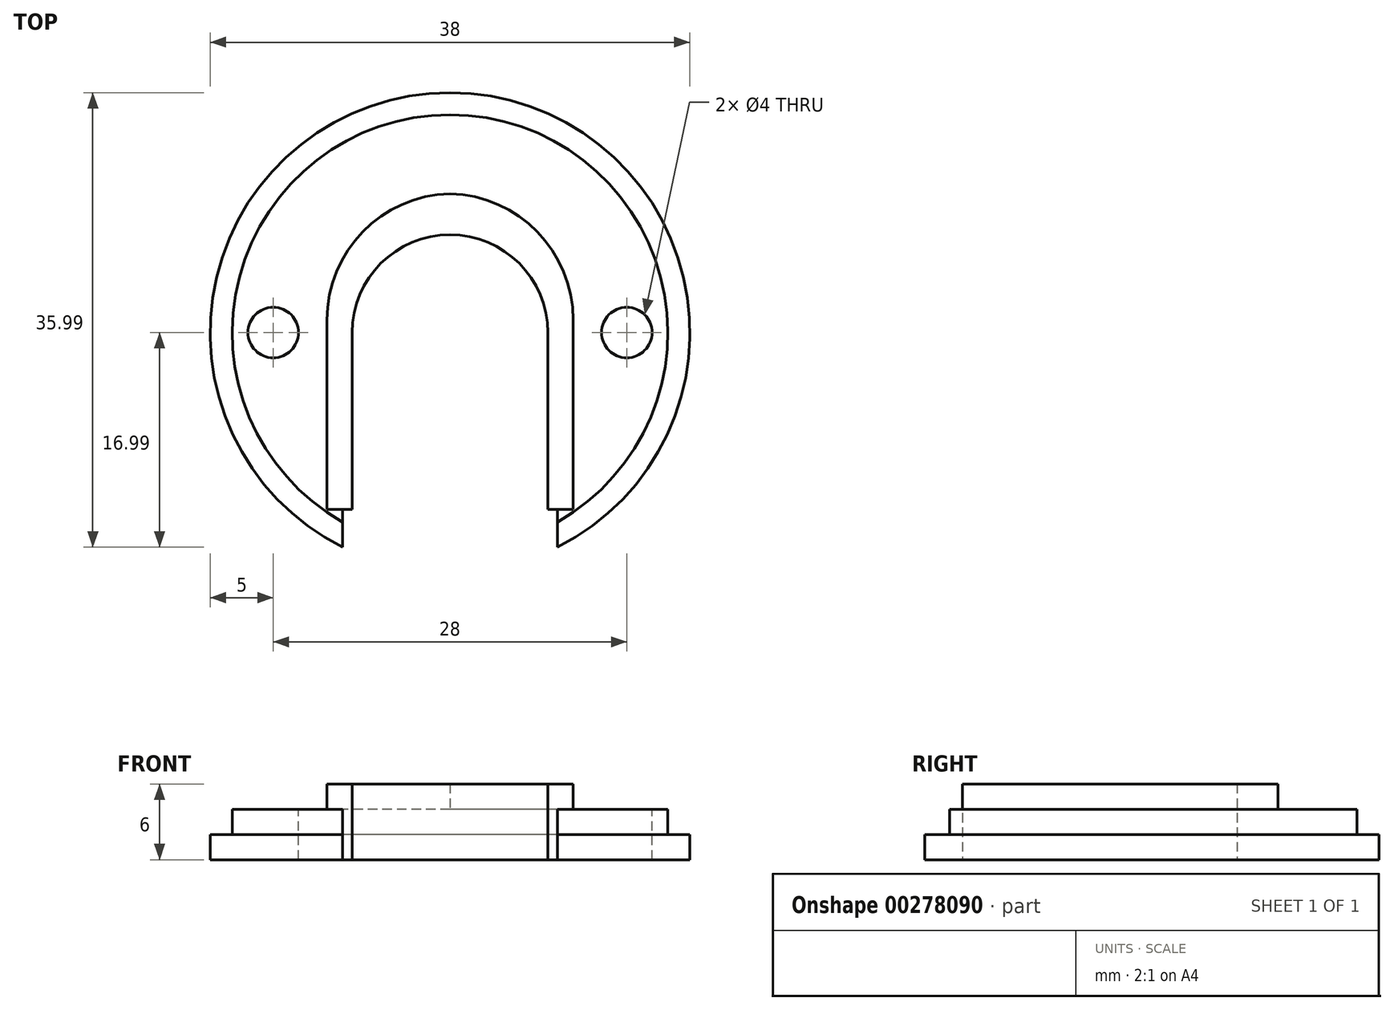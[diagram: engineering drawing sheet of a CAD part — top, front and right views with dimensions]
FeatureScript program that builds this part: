
annotation { "Feature Type Name" : "Feature", "Feature Type Description" : "" }
export const myFeature = defineFeature(function(context is Context, id is Id, definition is map)
    precondition{}
    {
        {
            var Q0;
            Q0=qCreatedBy(makeId("Top.planeOp"),FACE);
            var sketch = newSketch(context, id + "F0", { "sketchPlane" : qUnion([Q0])});
            skCircle(sketch, "E0", {"center": v(0, 0) * mm, "radius": 19 * mm});
            skSolve(sketch);
        }
        {
            var Q0;
            Q0=makeQuery(id+"F0.imprint","IMPRINT",FACE,{"disambiguationData":[TD([[makeQuery(id+"F0.imprint","IMPRINT",EDGE,{"derivedFrom":sQuery(id+"F0.wireOp",EDGE,"E0")}),1.0]])]});
            extrude(context, id + "F1", {"entities" : qUnion([Q0]), "depth" : 2 * mm});
        }
        {
            var Q0;
            Q0=makeQuery(id+"F1.opExtrude","CAP_FACE",FACE,{"disambiguationData":[OSD([sQuery(id+"F0.wireOp",EDGE,"E0")])],"isStart":false});
            var sketch = newSketch(context, id + "F2", { "sketchPlane" : qUnion([Q0])});
            skCircle(sketch, "E1", {"center": v(0, 0) * mm, "radius": 17.25 * mm});
            skSolve(sketch);
        }
        {
            var Q0;
            Q0=makeQuery(id+"F2.imprint","IMPRINT",FACE,{"disambiguationData":[TD([[makeQuery(id+"F2.imprint","IMPRINT",EDGE,{"derivedFrom":sQuery(id+"F2.wireOp",EDGE,"E1")}),1.0]])]});
            extrude(context, id + "F3", {"entities" : qUnion([Q0]), "operationType" : NewBodyOperationType.ADD, "depth" : 2 * mm});
        }
        {
            var Q0;
            Q0=makeQuery(id+"F3.opExtrude","CAP_FACE",FACE,{"disambiguationData":[OSD([sQuery(id+"F2.wireOp",EDGE,"E1")])],"isStart":false});
            var sketch = newSketch(context, id + "F4", { "sketchPlane" : qUnion([Q0])});
            skCircle(sketch, "E2", {"center": v(0, 0) * mm, "radius": 8.5 * mm});
            skLineSegment(sketch, "E3", {"start": v(0, 0) * mm, "end": v(8.5, 0) * mm});
            skLineSegment(sketch, "E4", {"start": v(0, 0) * mm, "end": v(-8.5, 0) * mm});
            skLineSegment(sketch, "E5", {"start": v(-8.5, 0) * mm, "end": v(-8.5, -31.09) * mm});
            skLineSegment(sketch, "E6", {"start": v(8.5, 0) * mm, "end": v(8.5, -31.97) * mm});
            skLineSegment(sketch, "E7", {"start": v(8.5, -31.97) * mm, "end": v(-8.5, -31.09) * mm});
            skSolve(sketch);
        }
        {
            var Q0;
            {var subQ0=sQuery(id+"F4.wireOp",EDGE,"E3");Q0=makeQuery(id+"F4.imprint","IMPRINT",FACE,{"disambiguationData":[TD([[makeQuery(id+"F4.imprint","IMPRINT",EDGE,{"derivedFrom":subQ0}),1.0]])]});}
            var Q1;
            {var subQ0=sQuery(id+"F4.wireOp",EDGE,"E3");Q1=makeQuery(id+"F4.imprint","IMPRINT",FACE,{"disambiguationData":[TD([[makeQuery(id+"F4.imprint","IMPRINT",EDGE,{"derivedFrom":subQ0}),-1.0]])]});}
            var Q2;
            {var subQ0=sQuery(id+"F4.wireOp",EDGE,"E7");Q2=makeQuery(id+"F4.imprint","IMPRINT",FACE,{"disambiguationData":[TD([[makeQuery(id+"F4.imprint","IMPRINT",EDGE,{"derivedFrom":subQ0}),-1.0]])]});}
            var Q3;
            {var subQ3=sQuery(id+"F4.wireOp",EDGE,"E5");var subQ5=makeQuery(id+"F3.opExtrude","CAP_EDGE",EDGE,{"disambiguationData":[OSD([sQuery(id+"F2.wireOp",EDGE,"E1")])],"isStart":false});var subQ6=makeQuery(id+"F4.imprint","INTERSECT",VERTEX,{"derivedFrom":[subQ5,subQ3]});Q3=makeQuery(id+"F4.imprint","IMPRINT",FACE,{"disambiguationData":[TD([[makeQuery(id+"F4.imprint","IMPRINT",EDGE,{"disambiguationData":[TD([[subQ6,-1.0]])],"derivedFrom":subQ5}),1.0]])]});}
            extrude(context, id + "F5", {"entities" : qUnion([Q0, Q1, Q2, Q3]), "operationType" : NewBodyOperationType.REMOVE, "oppositeDirection" : true, "depth" : 25 * mm});
        }
        {
            var Q0;
            Q0=qCreatedBy(makeId("Top.planeOp"),FACE);
            var sketch = newSketch(context, id + "F6", { "sketchPlane" : qUnion([Q0])});
            skCircle(sketch, "E8", {"center": v(0, 0) * mm, "radius": 7.75 * mm});
            skLineSegment(sketch, "E9", {"start": v(-7.75, 0) * mm, "end": v(7.75, 0) * mm});
            skLineSegment(sketch, "E10", {"start": v(-7.75, 0) * mm, "end": v(-7.75, -14) * mm});
            skLineSegment(sketch, "E11", {"start": v(-7.75, -14) * mm, "end": v(-9.75, -14) * mm});
            skLineSegment(sketch, "E12", {"start": v(-9.75, -14) * mm, "end": v(-9.75, 11) * mm});
            skLineSegment(sketch, "E13", {"start": v(7.75, 0) * mm, "end": v(7.75, -14) * mm});
            skLineSegment(sketch, "E14", {"start": v(7.75, -14) * mm, "end": v(9.75, -14) * mm});
            skLineSegment(sketch, "E15", {"start": v(9.75, -14) * mm, "end": v(9.75, 11) * mm});
            skLineSegment(sketch, "E16", {"start": v(9.75, 11) * mm, "end": v(-9.75, 11) * mm});
            skSolve(sketch);
        }
        {
            var Q0;
            {var subQ0=sQuery(id+"F6.wireOp",EDGE,"E10");Q0=makeQuery(id+"F6.imprint","IMPRINT",FACE,{"disambiguationData":[TD([[makeQuery(id+"F6.imprint","IMPRINT",EDGE,{"derivedFrom":subQ0}),-1.0]])]});}
            extrude(context, id + "F7", {"entities" : qUnion([Q0]), "operationType" : NewBodyOperationType.ADD, "depth" : 6 * mm});
        }
        {
            var Q0;
            Q0=makeQuery(id+"F7.opExtrude","SWEPT_EDGE",EDGE,{"disambiguationData":[OSD([sQuery(id+"F6.wireOp",EDGE,"E15"),sQuery(id+"F6.wireOp",EDGE,"E16")])]});
            var Q1;
            Q1=makeQuery(id+"F7.opExtrude","SWEPT_EDGE",EDGE,{"disambiguationData":[OSD([sQuery(id+"F6.wireOp",EDGE,"E12"),sQuery(id+"F6.wireOp",EDGE,"E16")])]});
            fillet(context, id + "F8", {"entities" : qUnion([Q0, Q1]), "radius" : 10 * mm, "tangentPropagation" : true, "allowEdgeOverflow" : false});
        }
        {
            var Q0;
            Q0=makeQuery(id+"F1.opExtrude","CAP_FACE",FACE,{"disambiguationData":[OSD([sQuery(id+"F0.wireOp",EDGE,"E0")])],"isStart":false});
            var sketch = newSketch(context, id + "F9", { "sketchPlane" : qUnion([Q0])});
            skLineSegment(sketch, "E17", {"start": v(-19, 0) * mm, "end": v(-14, 0) * mm});
            skLineSegment(sketch, "E18", {"start": v(19, 0) * mm, "end": v(14, 0) * mm});
            skCircle(sketch, "E19", {"center": v(14, 0) * mm, "radius": 2 * mm});
            skCircle(sketch, "E20", {"center": v(-14, 0) * mm, "radius": 2 * mm});
            skSolve(sketch);
        }
        {
            var Q0;
            Q0 = qSketchRegion(id + "F9", true);
            extrude(context, id + "F10", {"entities" : qUnion([Q0]), "operationType" : NewBodyOperationType.REMOVE, "oppositeDirection" : true, "depth" : 25 * mm});
        }
        {
            var Q0;
            Q0=makeQuery(id+"F10.boolean.opBoolean","COPY",FACE,{"derivedFrom":makeQuery(id+"F10.opExtrude","CAP_FACE",FACE,{"disambiguationData":[OSD([sQuery(id+"F9.wireOp",EDGE,"E20")])],"isStart":true})});
            var sketch = newSketch(context, id + "F11", { "sketchPlane" : qUnion([Q0])});
            skCircle(sketch, "E21", {"center": v(-14, 0) * mm, "radius": 2 * mm});
            skSolve(sketch);
        }
        {
            var Q0;
            Q0=makeQuery(id+"F11.imprint","IMPRINT",FACE,{"disambiguationData":[TD([[makeQuery(id+"F11.imprint","IMPRINT",EDGE,{"derivedFrom":sQuery(id+"F11.wireOp",EDGE,"E21")}),-1.0]])]});
            extrude(context, id + "F12", {"entities" : qUnion([Q0]), "operationType" : NewBodyOperationType.REMOVE, "oppositeDirection" : true, "depth" : 25 * mm});
        }
        {
            var Q0;
            Q0=makeQuery(id+"F10.boolean.opBoolean","COPY",FACE,{"derivedFrom":makeQuery(id+"F10.opExtrude","CAP_FACE",FACE,{"disambiguationData":[OSD([sQuery(id+"F9.wireOp",EDGE,"E19")])],"isStart":true})});
            var sketch = newSketch(context, id + "F13", { "sketchPlane" : qUnion([Q0])});
            skCircle(sketch, "E22", {"center": v(14, 0) * mm, "radius": 2 * mm});
            skSolve(sketch);
        }
        {
            var Q0;
            Q0=makeQuery(id+"F13.imprint","IMPRINT",FACE,{"disambiguationData":[TD([[makeQuery(id+"F13.imprint","IMPRINT",EDGE,{"derivedFrom":sQuery(id+"F13.wireOp",EDGE,"E22")}),-1.0]])]});
            extrude(context, id + "F14", {"entities" : qUnion([Q0]), "operationType" : NewBodyOperationType.REMOVE, "oppositeDirection" : true, "depth" : 25 * mm});
        }
    });
